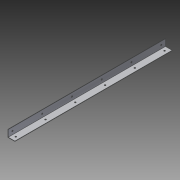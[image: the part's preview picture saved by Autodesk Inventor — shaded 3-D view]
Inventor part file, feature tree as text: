
AUTODESK INVENTOR PART (.ipt)
format: ipt  version: 2014 SP1 (Build 180222100, 222)  size: 110,592 bytes
history: native  units: in
note: dims shown in document units (in); Inventor stores cm internally (conversion verified against a paired STEP export)
features: extrude x3, sketch x3
ambient origin geometry x8: Origin, YZ Plane, XZ Plane, XY Plane, X Axis, Y Axis, Z Axis, Center Point
bodies: Solid1 (feature_tree)
feature tree (6):
  extrude  "Extrusion1"  Depth=0.0312in
  sketch  "Sketch2"  dims[d2=14.0in d3=0.0in d4=0.375in]
  sketch  "Sketch3"  dims[d5=0.125in d6=14.0in d7=2.3622in d9=2.65in d10=0.3937in d12=1.0in d14=0.125in d15=0.375in d16=14.0in d17=2.3622in d19=2.65in d20=0.3937in d22=1.0in d24=1.0in d25=0.0in d26=1.0in d27=0.0in]
  extrude  "Extrusion2"  Depth=14.0in
  extrude  "Extrusion3"  Depth=14.0in
  sketch  "Sketch1"  dims[d0=0.625in d1=0.0312in]
